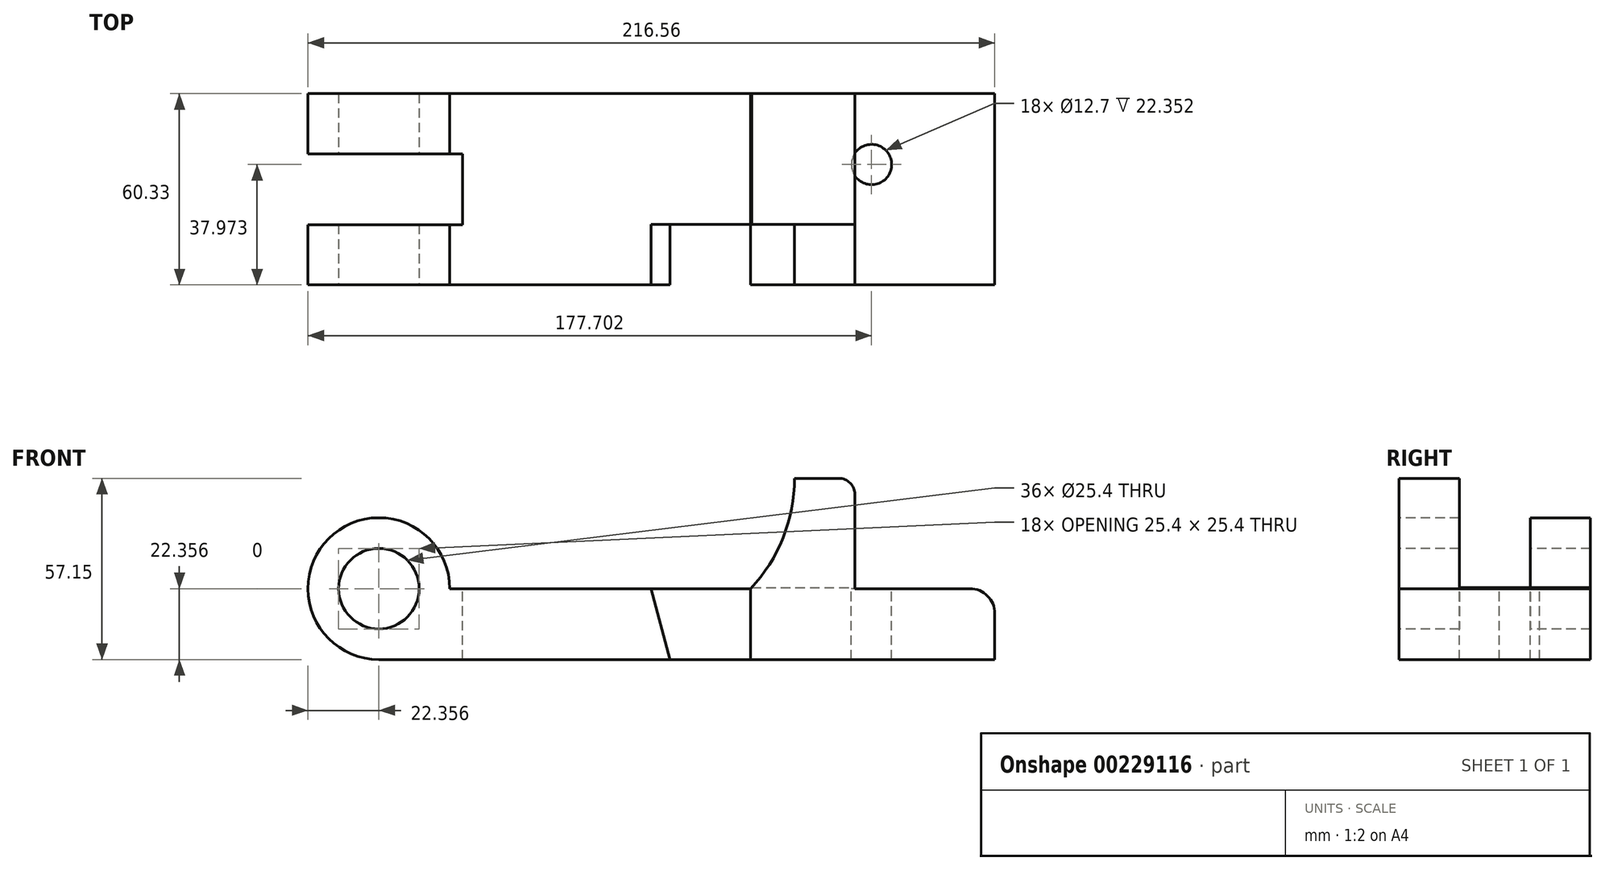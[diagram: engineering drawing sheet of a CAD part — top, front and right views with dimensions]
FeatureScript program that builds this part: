
annotation { "Feature Type Name" : "Feature", "Feature Type Description" : "" }
export const myFeature = defineFeature(function(context is Context, id is Id, definition is map)
    precondition{}
    {
        {
            var Q0;
            Q0=qCreatedBy(makeId("Front.planeOp"),FACE);
            var sketch = newSketch(context, id + "F0", { "sketchPlane" : qUnion([Q0])});
            skLineSegment(sketch, "E0.bottom", {"start": v(97.1, -11.18) * mm, "end": v(-97.1, -11.18) * mm});
            skLineSegment(sketch, "E0.top", {"start": v(97.1, 11.18) * mm, "end": v(52.98, 11.18) * mm});
            skLineSegment(sketch, "E0.left", {"start": v(97.1, -11.18) * mm, "end": v(97.1, 11.18) * mm});
            skLineSegment(sketch, "E0.right", {"start": v(-97.1, -11.18) * mm, "end": v(-97.1, 11.18) * mm});
            skPoint(sketch, "E0.middle", {"position": v(0, 0) * mm});
            skCircle(sketch, "E1", {"center": v(-97.1, 11.18) * mm, "radius": 12.7 * mm});
            skCircle(sketch, "E2", {"center": v(-97.1, 11.18) * mm, "radius": 22.35 * mm});
            skLineSegment(sketch, "E3", {"start": v(-11.25, 11.18) * mm, "end": v(-5.26, -11.18) * mm});
            skLineSegment(sketch, "E4", {"start": v(20.14, -11.18) * mm, "end": v(20.14, 11.18) * mm});
            skLineSegment(sketch, "E5", {"start": v(52.98, 11.18) * mm, "end": v(52.98, 45.97) * mm});
            skLineSegment(sketch, "E6", {"start": v(52.98, 45.97) * mm, "end": v(33.93, 45.97) * mm});
            skArc(sketch, "E7", {"start": v(20.14, 11.18) * mm, "mid": v(30.36, 27.26) * mm, "end": v(33.93, 45.97) * mm});
            skLineSegment(sketch, "E8.trimOffspring", {"start": v(20.14, 11.18) * mm, "end": v(-97.1, 11.18) * mm});
            skSolve(sketch);
        }
        {
            var Q0;
            Q0 = qSketchRegion(id + "F0", true);
            extrude(context, id + "F1", {"entities" : qUnion([Q0]), "oppositeDirection" : true, "depth" : 60.32 * mm});
        }
        {
            var Q0;
            Q0=qCreatedBy(makeId("Top.planeOp"),FACE);
            var sketch = newSketch(context, id + "F2", { "sketchPlane" : qUnion([Q0])});
            skLineSegment(sketch, "E9.bottom", {"start": v(-70.72, 41.33) * mm, "end": v(-123.73, 41.33) * mm});
            skLineSegment(sketch, "E9.top", {"start": v(-70.72, 19) * mm, "end": v(-123.73, 19) * mm});
            skLineSegment(sketch, "E9.left", {"start": v(-70.72, 41.33) * mm, "end": v(-70.72, 19) * mm});
            skLineSegment(sketch, "E9.right", {"start": v(-123.73, 41.33) * mm, "end": v(-123.73, 19) * mm});
            skSolve(sketch);
        }
        {
            var Q0;
            Q0=makeQuery(id+"F2.imprint","IMPRINT",FACE,{"disambiguationData":[TD([[makeQuery(id+"F2.imprint","IMPRINT",EDGE,{"derivedFrom":sQuery(id+"F2.wireOp",EDGE,"E9.bottom")}),1.0]])]});
            extrude(context, id + "F3", {"entities" : qUnion([Q0]), "operationType" : NewBodyOperationType.REMOVE, "endBound" : BoundingType.SYMMETRIC, "oppositeDirection" : true, "depth" : 88.53 * mm});
        }
        {
            var Q0;
            Q0=qCreatedBy(makeId("Right.planeOp"),FACE);
            var sketch = newSketch(context, id + "F4", { "sketchPlane" : qUnion([Q0])});
            skLineSegment(sketch, "E10.bottom", {"start": v(60.96, 11.49) * mm, "end": v(19.05, 11.49) * mm});
            skLineSegment(sketch, "E10.top", {"start": v(60.96, 46.16) * mm, "end": v(19.05, 46.16) * mm});
            skLineSegment(sketch, "E10.left", {"start": v(60.96, 11.49) * mm, "end": v(60.96, 46.16) * mm});
            skLineSegment(sketch, "E10.right", {"start": v(19.05, 11.49) * mm, "end": v(19.05, 46.16) * mm});
            skSolve(sketch);
        }
        {
            var Q0;
            Q0 = qSketchRegion(id + "F4", true);
            extrude(context, id + "F5", {"entities" : qUnion([Q0]), "operationType" : NewBodyOperationType.REMOVE, "depth" : 77.5 * mm});
        }
        {
            var Q0;
            Q0=makeQuery(id+"F1.opExtrude","SWEPT_EDGE",EDGE,{"disambiguationData":[OSD([sQuery(id+"F0.wireOp",EDGE,"E0.top"),sQuery(id+"F0.wireOp",EDGE,"E0.left")])]});
            fillet(context, id + "F6", {"entities" : qUnion([Q0]), "radius" : 7.87 * mm, "tangentPropagation" : true, "allowEdgeOverflow" : false});
        }
        {
            var Q0;
            Q0=makeQuery(id+"F1.opExtrude","SWEPT_EDGE",EDGE,{"disambiguationData":[OSD([sQuery(id+"F0.wireOp",EDGE,"E5"),sQuery(id+"F0.wireOp",EDGE,"E6")])]});
            fillet(context, id + "F7", {"entities" : qUnion([Q0]), "radius" : 5.08 * mm, "tangentPropagation" : true, "allowEdgeOverflow" : false});
        }
        {
            var Q0;
            {var subQ0=sQuery(id+"F0.wireOp",EDGE,"E3");Q0=makeQuery(id+"F0.imprint","IMPRINT",FACE,{"disambiguationData":[TD([[makeQuery(id+"F0.imprint","IMPRINT",EDGE,{"derivedFrom":subQ0}),1.0]])]});}
            extrude(context, id + "F8", {"entities" : qUnion([Q0]), "operationType" : NewBodyOperationType.REMOVE, "oppositeDirection" : true, "depth" : 19.05 * mm});
        }
        {
            var Q0;
            Q0=makeQuery(id+"F1.opExtrude","SWEPT_FACE",FACE,{"disambiguationData":[OSD([sQuery(id+"F0.wireOp",EDGE,"E0.top")])]});
            var sketch = newSketch(context, id + "F9", { "sketchPlane" : qUnion([Q0])});
            skCircle(sketch, "E11", {"center": v(58.24, 37.97) * mm, "radius": 6.35 * mm});
            skSolve(sketch);
        }
        {
            var Q0;
            Q0 = qSketchRegion(id + "F9", true);
            extrude(context, id + "F10", {"entities" : qUnion([Q0]), "operationType" : NewBodyOperationType.REMOVE, "endBound" : BoundingType.THROUGH_ALL, "oppositeDirection" : true, "depth" : 25.4 * mm});
        }
    });
